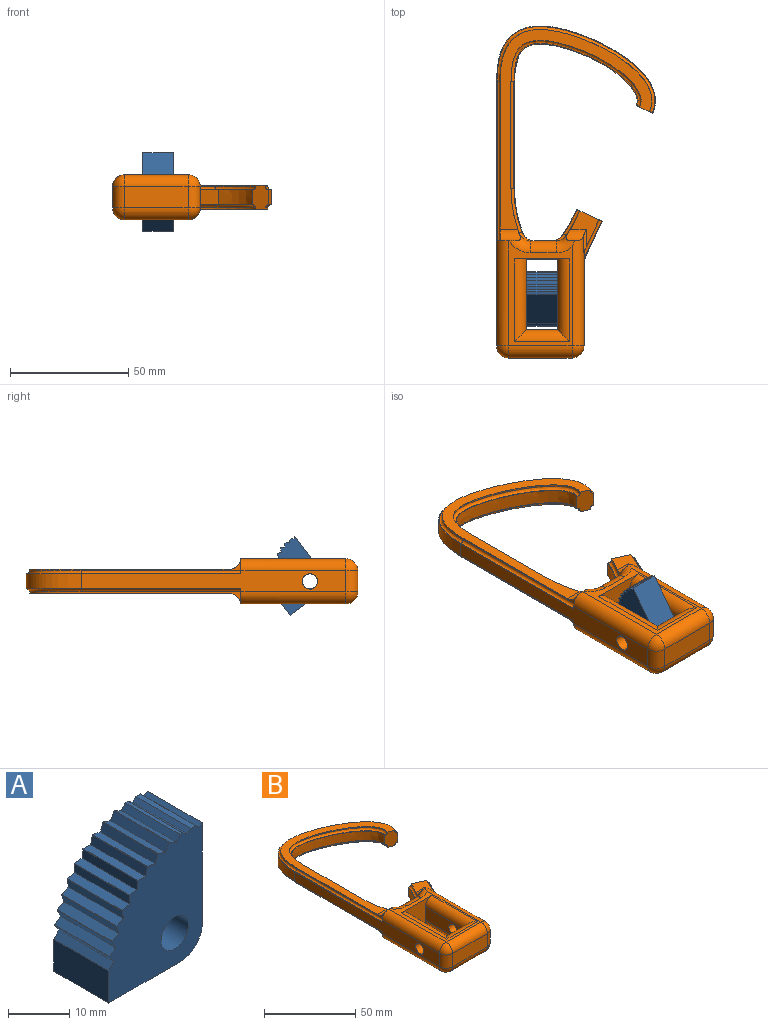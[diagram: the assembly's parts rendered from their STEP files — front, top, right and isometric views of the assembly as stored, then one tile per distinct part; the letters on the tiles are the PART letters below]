
ASSEMBLY  parts=2 mates=1
PART A: 42 faces, bbox 21.6x12.7x25.4 mm
  f0: plane 12.7x0.65mm, normal (0,0,1), area 8.3mm2, adj f15,f16,f21,f22
  f1: cylinder r=19.53mm len=12.7mm, axis (0,1,0), area 0.8mm2, adj f15,f16,f37,f38
  f2: cylinder r=19.53mm len=12.7mm, axis (0,1,0), area 0.8mm2, adj f15,f16,f27,f36
  f3: cylinder r=19.53mm len=12.7mm, axis (0,1,0), area 0.8mm2, adj f15,f16,f33,f34
  f4: cylinder r=19.53mm len=12.7mm, axis (0,1,0), area 0.8mm2, adj f15,f16,f32,f39
  f5: cylinder r=19.53mm len=12.7mm, axis (0,1,0), area 0.8mm2, adj f15,f16,f29,f30
  f6: cylinder r=19.53mm len=12.7mm, axis (0,1,0), area 0.8mm2, adj f15,f16,f28,f40
  f7: cylinder r=19.53mm len=12.7mm, axis (0,1,0), area 0.8mm2, adj f15,f16,f25,f26
  f8: cylinder r=19.53mm len=12.7mm, axis (0,1,0), area 0.8mm2, adj f15,f16,f24,f31
  f9: plane 12.7x1.05mm, normal (0,0,1), area 13.3mm2, adj f15,f16,f18,f23
  f10: cylinder r=19.53mm len=12.7mm, axis (0,1,0), area 0.8mm2, adj f15,f16,f20,f35
  f11: plane 12.7x6.39mm, normal (-1,0,0), area 81.2mm2, adj f12,f15,f16,f41
  f12: plane 16.51x12.7mm, normal (0,0,-1), area 209.7mm2, adj f11,f15,f16,f17
  f13: cylinder r=3.17mm len=12.7mm, axis (0,1,0), area 253.4mm2, adj f15,f16
  f14: plane 20.17x12.7mm, normal (1,0,0), area 256.2mm2, adj f15,f16,f17,f19
  f15: plane 25.44x21.59mm, normal (0,-1,0), area 420.5mm2, adj f0,f1,f2,f3,f4,f5,f6,f7
  f16: plane 25.44x21.59mm, normal (0,1,0), area 420.5mm2, adj f0,f1,f2,f3,f4,f5,f6,f7
  f17: cylinder r=5.08mm len=12.7mm, axis (0,1,0), area 101.3mm2, adj f12,f14,f15,f16
  f18: plane 12.7x0.79mm, normal (0.69,0,0.72), area 13.9mm2, adj f9,f15,f16,f19
  f19: plane 12.7x0.78mm, normal (-0.59,0,0.81), area 12.3mm2, adj f14,f15,f16,f18
  f20: plane 12.7x1.58mm, normal (0.46,0,0.89), area 22.6mm2, adj f10,f15,f16,f21
  f21: plane 12.7x1.14mm, normal (-0.79,0,0.61), area 18.3mm2, adj f0,f15,f16,f20
  f22: plane 12.7x1.06mm, normal (0.59,0,0.81), area 16.6mm2, adj f0,f15,f16,f23
  f23: plane 12.7x0.79mm, normal (-0.7,0,0.72), area 13.9mm2, adj f9,f15,f16,f22
  f24: plane 12.7x1.65mm, normal (-0.37,0,0.93), area 22.6mm2, adj f8,f15,f16,f25
  f25: plane 12.7x1.74mm, normal (-0.98,0,-0.2), area 22.6mm2, adj f7,f15,f16,f24
  f26: plane 12.7x1.73mm, normal (-0.23,0,0.97), area 22.6mm2, adj f7,f15,f16,f27
  f27: plane 12.7x1.78mm, normal (-1,0,-0.06), area 22.6mm2, adj f2,f15,f16,f26
  f28: plane 12.7x1.4mm, normal (-0.61,0,0.79), area 22.6mm2, adj f6,f15,f16,f29
  f29: plane 12.7x1.57mm, normal (-0.88,0,-0.47), area 22.6mm2, adj f5,f15,f16,f28
  f30: plane 12.7x1.55mm, normal (-0.49,0,0.87), area 22.6mm2, adj f5,f15,f16,f31
  f31: plane 12.7x1.67mm, normal (-0.94,0,-0.34), area 22.6mm2, adj f8,f15,f16,f30
  f32: plane 12.7x1.74mm, normal (0.2,0,0.98), area 22.6mm2, adj f4,f15,f16,f33
  f33: plane 12.7x1.66mm, normal (-0.93,0,0.36), area 22.6mm2, adj f3,f15,f16,f32
  f34: plane 12.7x1.68mm, normal (0.33,0,0.94), area 22.6mm2, adj f3,f15,f16,f35
  f35: plane 12.7x1.55mm, normal (-0.87,0,0.49), area 22.6mm2, adj f10,f15,f16,f34
  f36: plane 12.7x1.77mm, normal (-0.09,0,1), area 22.6mm2, adj f2,f15,f16,f37
  f37: plane 12.7x1.77mm, normal (-1,0,0.09), area 22.6mm2, adj f1,f15,f16,f36
  f38: plane 12.7x1.78mm, normal (0.05,0,1), area 22.6mm2, adj f1,f15,f16,f39
  f39: plane 12.7x1.73mm, normal (-0.97,0,0.23), area 22.6mm2, adj f4,f15,f16,f38
  f40: plane 12.7x1.44mm, normal (-0.81,0,-0.59), area 22.6mm2, adj f6,f15,f16,f41
  f41: plane 12.7x1.28mm, normal (-0.72,0,0.69), area 22.6mm2, adj f11,f15,f16,f40
PART B: 104 faces, bbox 71.7x144.6x20.2 mm
  f0: plane 29.93x8.89mm, normal (-1,0,0), area 232.6mm2, adj f13,f28,f65,f74,f77
  f1: plane 11.41x6.75mm, normal (0,0,1), area 3.2mm2, adj f11,f12,f66,f93,f94
  f2: plane 11.41x6.75mm, normal (0,0,-1), area 3.2mm2, adj f11,f12,f66,f90,f91
  f3: plane 94x70.25mm, normal (0,0,1), area 42.7mm2, adj f7,f18,f19,f25,f96,f97
  f4: plane 94x70.25mm, normal (0,0,-1), area 42.7mm2, adj f7,f18,f19,f23,f98,f99
  f5: plane 16.51x7.65mm, normal (0,0,1), area 4.5mm2, adj f9,f10,f11,f103
  f6: plane 16.51x7.65mm, normal (0,0,-1), area 4.5mm2, adj f9,f10,f11,f102
  f7: plane 111.88x8.89mm, normal (-1,0,0), area 789.7mm2, adj f3,f4,f19,f23,f25,f27,f53,f55
  f8: plane 26.81x8.89mm, normal (0,-1,0), area 238.4mm2, adj f56,f57,f61,f62
  f9: plane 40.99x10.04mm, normal (1,0,0), area 296.2mm2, adj f5,f6,f10,f28,f58,f62,f64,f102
  f10: plane 16.4x7.65mm, normal (0.91,-0.42,0), area 114.9mm2, adj f5,f6,f9,f11
  f11: plane 10.78x7.63mm, normal (0.42,0.91,0), area 75.8mm2, adj f1,f2,f5,f6,f10,f12,f44,f45
  f12: extruded ~11.22x6.38mm, area 82.1mm2, adj f1,f2,f11,f66
  f13: plane 13.21x8.89mm, normal (0,1,0), area 117.4mm2, adj f0,f14,f75,f78
  f14: plane 29.93x8.89mm, normal (1,0,0), area 232.6mm2, adj f13,f27,f65,f76,f79
  f15: cylinder r=51.03mm len=18.79mm, axis (0,0,-1), area 122.2mm2, adj f16,f20,f21,f67
  f16: plane 45.52x6.35mm, normal (1,0,0), area 289.1mm2, adj f15,f17,f20,f21
  f17: extruded ~51.89x25.99mm, area 470.6mm2, adj f16,f18,f20,f21
  f18: plane 10.2x6.95mm, normal (-0.42,-0.91,0), area 67.2mm2, adj f3,f4,f17,f19,f20,f21,f29,f32
  f19: extruded ~67.13x36.82mm, area 643.7mm2, adj f3,f4,f7,f18
  f20: plane 81.13x52.41mm, normal (0,0,1), area 35.4mm2, adj f15,f16,f17,f18,f67,f85,f86,f87
  f21: plane 81.13x52.41mm, normal (0,0,-1), area 35.4mm2, adj f15,f16,f17,f18,f67,f80,f81,f82
  f22: plane 44.36x26.81mm, normal (0,0,-1), area 255.3mm2, adj f51,f55,f61,f64,f65,f71,f72,f73
  f23: plane 4.9x1.52mm, normal (0,1,0), area 5.4mm2, adj f4,f7,f38,f55,f99
  f24: plane 8.89x7.45mm, normal (0,1,0), area 66.3mm2, adj f66,f67,f69,f72
  f25: plane 4.9x1.52mm, normal (0,1,0), area 5.4mm2, adj f3,f7,f31,f53,f97
  f26: plane 44.36x26.81mm, normal (0,0,1), area 255.3mm2, adj f52,f53,f57,f58,f65,f68,f69,f70
  f27: cylinder r=3.26mm len=12.61mm, axis (1,0,0), area 258.5mm2, adj f7,f14
  f28: cylinder r=3.26mm len=11.16mm, axis (1,0,0), area 228.9mm2, adj f0,f9
  f29: plane 84.27x64.11mm, normal (0,0,1), area 702.5mm2, adj f18,f30,f31,f32,f33,f34,f52
  f30: cylinder r=52.55mm len=18.73mm, axis (0,0,-1), area 12mm2, adj f29,f34,f52,f70,f87
  f31: plane 67.52x3.63mm, normal (-1,0,0), area 48mm2, adj f25,f29,f32,f52,f53,f97
  f32: extruded ~64.08x34.66mm, area 60.9mm2, adj f18,f29,f31,f96
  f33: extruded ~54.94x28.16mm, area 50.5mm2, adj f18,f29,f34,f85
  f34: plane 45.52x0.64mm, normal (1,0,0), area 28.9mm2, adj f29,f30,f33,f86
  f35: plane 45.52x0.64mm, normal (1,0,0), area 28.9mm2, adj f36,f39,f40,f81
  f36: extruded ~54.94x28.16mm, area 50.5mm2, adj f18,f35,f40,f80
  f37: extruded ~64.08x34.66mm, area 60.9mm2, adj f18,f38,f40,f98
  f38: plane 67.52x3.63mm, normal (-1,0,0), area 48mm2, adj f23,f37,f40,f51,f55,f99
  f39: cylinder r=52.55mm len=18.73mm, axis (0,0,-1), area 12mm2, adj f35,f40,f51,f73,f82
  f40: plane 84.27x64.11mm, normal (0,0,-1), area 702.5mm2, adj f18,f35,f36,f37,f38,f39,f51
  f41: plane 15.07x12.01mm, normal (0,0,1), area 70mm2, adj f42,f43,f44,f50,f100
  f42: extruded ~10.45x5.79mm, area 7.9mm2, adj f41,f44,f50,f68,f93
  f43: plane 14.58x7.14mm, normal (0.91,-0.42,0), area 9.9mm2, adj f41,f44,f58,f100,f103
  f44: plane 10.35x4.85mm, normal (0.42,0.91,0), area 17.5mm2, adj f11,f41,f42,f43,f93,f103
  f45: plane 9.2x4.31mm, normal (0.42,0.91,0), area 17.2mm2, adj f11,f46,f47,f48,f90
  f46: plane 14.58x7.14mm, normal (0.91,-0.42,0), area 9.9mm2, adj f45,f47,f64,f101,f102
  f47: plane 15.07x12.01mm, normal (0,0,-1), area 70mm2, adj f45,f46,f48,f49,f101
  f48: extruded ~10.45x5.79mm, area 7.9mm2, adj f45,f47,f49,f71,f90
  f49: cylinder r=5.08mm len=8.56mm, axis (1,0,0), area 41.4mm2, adj f47,f48,f64,f71,f101
  f50: cylinder r=5.08mm len=8.56mm, axis (1,0,0), area 41.4mm2, adj f41,f42,f58,f68,f100
  f51: cylinder r=5.08mm len=8.63mm, axis (1,0,0), area 56.3mm2, adj f22,f38,f39,f40,f55,f73
  f52: cylinder r=5.08mm len=8.63mm, axis (1,0,0), area 56.3mm2, adj f26,f29,f30,f31,f53,f70
  f53: cylinder r=5.08mm len=44.77mm, axis (0,1,0), area 354.8mm2, adj f7,f25,f26,f31,f52,f54
  f54: sphere r=5.08mm, area 40.5mm2, adj f53,f56,f57
  f55: cylinder r=5.08mm len=44.77mm, axis (0,-1,0), area 354.8mm2, adj f7,f22,f23,f38,f51,f59
  f56: cylinder r=5.08mm len=8.89mm, axis (0,0,1), area 70.9mm2, adj f7,f8,f54,f59
  f57: cylinder r=5.08mm len=26.81mm, axis (-1,0,0), area 214mm2, adj f8,f26,f54,f60
  f58: cylinder r=5.08mm len=46.53mm, axis (0,-1,0), area 351.2mm2, adj f9,f26,f43,f50,f60,f68,f100
  f59: sphere r=5.08mm, area 40.5mm2, adj f55,f56,f61
  f60: sphere r=5.08mm, area 40.5mm2, adj f57,f58,f62
  f61: cylinder r=5.08mm len=26.81mm, axis (1,0,0), area 214mm2, adj f8,f22,f59,f63
  f62: cylinder r=5.08mm len=8.89mm, axis (0,0,-1), area 70.9mm2, adj f8,f9,f60,f63
  f63: sphere r=5.08mm, area 25.8mm2, adj f61,f62,f64
  f64: cylinder r=5.08mm len=46.53mm, axis (0,1,0), area 351.2mm2, adj f9,f22,f46,f49,f63,f71,f101
  f65: plane 23.37x19.05mm, normal (0,-1,0), area 273.8mm2, adj f0,f14,f22,f26,f74,f76,f77,f79
  f66: cylinder r=5.08mm len=8.89mm, axis (0,0,-1), area 34mm2, adj f1,f2,f12,f24,f91,f92,f94,f95
  f67: cylinder r=5.08mm len=8.89mm, axis (0,0,-1), area 43.1mm2, adj f15,f20,f21,f24,f83,f84,f88,f89
  f68: torus R=10.16mm, axis (0,0,1), area 49.1mm2, adj f26,f42,f50,f58,f69,f94
  f69: cylinder r=5.08mm len=10.96mm, axis (1,0,0), area 87.4mm2, adj f24,f26,f68,f70,f89,f95
  f70: torus R=10.16mm, axis (0,0,1), area 51.8mm2, adj f26,f30,f52,f69,f88
  f71: torus R=10.16mm, axis (0,0,1), area 49.1mm2, adj f22,f48,f49,f64,f72,f91
  f72: cylinder r=5.08mm len=10.96mm, axis (-1,0,0), area 87.4mm2, adj f22,f24,f71,f73,f84,f92
  f73: torus R=10.16mm, axis (0,0,1), area 51.8mm2, adj f22,f39,f51,f72,f83
  f74: cylinder r=5.08mm len=35.01mm, axis (0,-1,0), area 259.1mm2, adj f0,f22,f65,f75
  f75: cylinder r=5.08mm len=23.37mm, axis (-1,0,0), area 145.9mm2, adj f13,f22,f74,f76
  f76: cylinder r=5.08mm len=35.01mm, axis (0,-1,0), area 259.1mm2, adj f14,f22,f65,f75
  f77: cylinder r=5.08mm len=35.01mm, axis (0,1,0), area 259.1mm2, adj f0,f26,f65,f78
  f78: cylinder r=5.08mm len=23.37mm, axis (1,0,0), area 145.9mm2, adj f13,f26,f77,f79
  f79: cylinder r=5.08mm len=35.01mm, axis (0,1,0), area 259.1mm2, adj f14,f26,f65,f78
  f80: bspline ~54.95x52.23mm, area 155.4mm2, adj f18,f21,f36,f81
  f81: cylinder r=1.27mm len=45.52mm, axis (0,1,0), area 90.8mm2, adj f21,f35,f80,f82
  f82: torus R=51.28mm, axis (0,0,1), area 37.9mm2, adj f21,f39,f81,f83
  f83: torus R=3.81mm, axis (0,0,1), area 9.3mm2, adj f21,f67,f73,f82,f84
  f84: cylinder r=1.27mm len=1.64mm, axis (-1,0,0), area 0.7mm2, adj f67,f72,f83
  f85: bspline ~54.96x52.23mm, area 155.4mm2, adj f18,f20,f33,f86
  f86: cylinder r=1.27mm len=45.52mm, axis (0,-1,0), area 90.8mm2, adj f20,f34,f85,f87
  f87: torus R=51.28mm, axis (0,0,1), area 37.9mm2, adj f20,f30,f86,f88
  f88: torus R=3.81mm, axis (0,0,1), area 9.3mm2, adj f20,f67,f70,f87,f89
  f89: cylinder r=1.27mm len=1.64mm, axis (1,0,0), area 0.7mm2, adj f67,f69,f88
  f90: bspline ~12.93x8.03mm, area 23.7mm2, adj f2,f45,f48,f91
  f91: torus R=3.81mm, axis (0,0,1), area 7.7mm2, adj f2,f66,f71,f90,f92
  f92: cylinder r=1.27mm len=1.87mm, axis (-1,0,0), area 0.9mm2, adj f66,f72,f91
  f93: bspline ~12.93x8.03mm, area 23.7mm2, adj f1,f42,f44,f94
  f94: torus R=3.81mm, axis (0,0,1), area 7.7mm2, adj f1,f66,f68,f93,f95
  f95: cylinder r=1.27mm len=1.87mm, axis (1,0,0), area 0.9mm2, adj f66,f69,f94
  f96: bspline ~66.63x43.12mm, area 194.7mm2, adj f3,f18,f32,f97
  f97: cylinder r=1.27mm len=67.52mm, axis (0,1,0), area 134.7mm2, adj f3,f25,f31,f96
  f98: bspline ~66.63x43.11mm, area 194.7mm2, adj f4,f18,f37,f99
  f99: cylinder r=1.27mm len=67.52mm, axis (0,-1,0), area 134.7mm2, adj f4,f23,f38,f98
  f100: cylinder r=1.27mm len=10.06mm, axis (0,-1,0), area 11.8mm2, adj f41,f43,f50,f58
  f101: cylinder r=1.27mm len=10.06mm, axis (0,1,0), area 11.8mm2, adj f46,f47,f49,f64
  f102: cylinder r=1.27mm len=16.44mm, axis (0.42,0.91,0), area 32.3mm2, adj f6,f9,f11,f46
  f103: cylinder r=1.27mm len=16.44mm, axis (-0.42,-0.91,0), area 32.3mm2, adj f5,f9,f43,f44
PLACE A rot(axis=(-0.3,-0.3,-0.9),95.8deg) t=(-1.42,-35.63,15.08)mm
PLACE B t=(-20.63,-8.45,15.08)mm fixed
MATE revolute A.f13 <-> B.f27  axis (1,0,0) through (4.93,-35.63,15.08)mm
